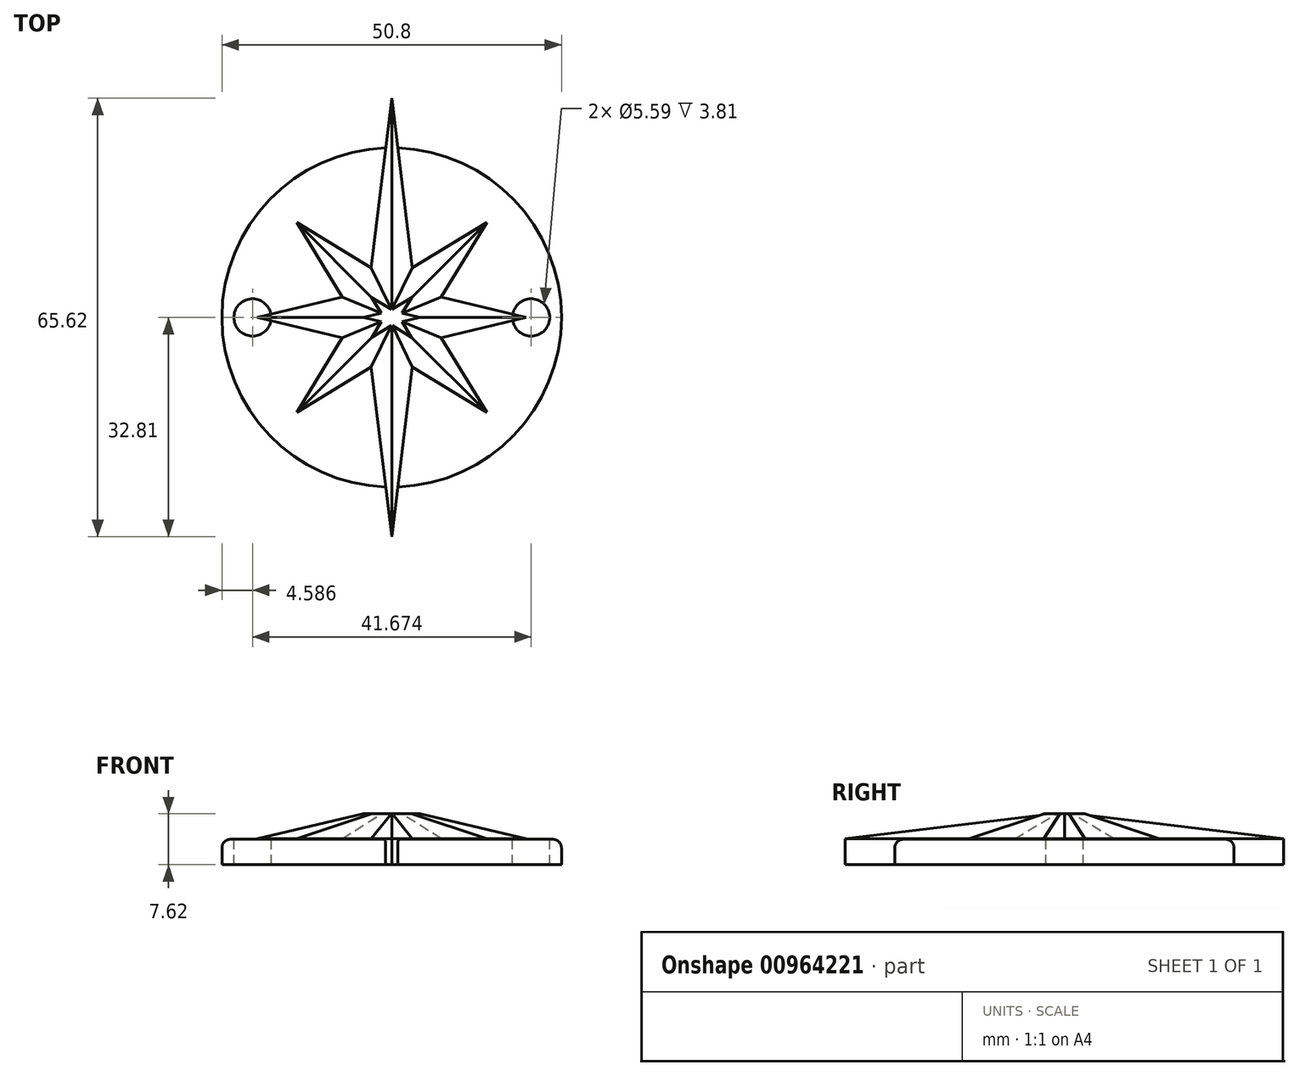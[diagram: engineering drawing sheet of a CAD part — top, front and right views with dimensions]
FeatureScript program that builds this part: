
annotation { "Feature Type Name" : "Feature", "Feature Type Description" : "" }
export const myFeature = defineFeature(function(context is Context, id is Id, definition is map)
    precondition{}
    {
        {
            var Q0;
            Q0=qCreatedBy(makeId("Top.planeOp"),FACE);
            var sketch = newSketch(context, id + "F0", { "sketchPlane" : qUnion([Q0])});
            skCircle(sketch, "E0.cCircle", {"center": v(0, 0) * mm, "radius": 7.42 * mm, "construction": true});
            skLineSegment(sketch, "E0.0", {"start": v(3.07, 7.42) * mm, "end": v(7.42, 3.07) * mm});
            skLineSegment(sketch, "E0.1", {"start": v(7.42, 3.07) * mm, "end": v(7.42, -3.07) * mm});
            skLineSegment(sketch, "E0.2", {"start": v(7.42, -3.07) * mm, "end": v(3.07, -7.42) * mm});
            skLineSegment(sketch, "E0.3", {"start": v(3.07, -7.42) * mm, "end": v(-3.07, -7.42) * mm});
            skLineSegment(sketch, "E0.4", {"start": v(-3.07, -7.42) * mm, "end": v(-7.42, -3.07) * mm});
            skLineSegment(sketch, "E0.5", {"start": v(-7.42, -3.07) * mm, "end": v(-7.42, 3.07) * mm});
            skLineSegment(sketch, "E0.6", {"start": v(-7.42, 3.07) * mm, "end": v(-3.07, 7.42) * mm});
            skLineSegment(sketch, "E0.7", {"start": v(-3.07, 7.42) * mm, "end": v(3.07, 7.42) * mm});
            skPoint(sketch, "E0.0.midPoint", {"position": v(5.24, 5.24) * mm});
            skSolve(sketch);
        }
        {
            var Q0;
            Q0=qCreatedBy(makeId("Top.planeOp"),FACE);
            var sketch = newSketch(context, id + "F1", { "sketchPlane" : qUnion([Q0])});
            skLineSegment(sketch, "E1", {"start": v(0, -32.8) * mm, "end": v(3.07, -7.42) * mm});
            skLineSegment(sketch, "E2", {"start": v(3.07, -7.42) * mm, "end": v(14.23, -14.23) * mm});
            skLineSegment(sketch, "E3", {"start": v(14.23, -14.23) * mm, "end": v(7.4, -3.07) * mm});
            skLineSegment(sketch, "E4", {"start": v(7.4, -3.07) * mm, "end": v(20.12, 0) * mm});
            skLineSegment(sketch, "E5", {"start": v(20.12, 0) * mm, "end": v(7.42, 3.07) * mm});
            skLineSegment(sketch, "E6", {"start": v(7.42, 3.07) * mm, "end": v(14.22, 14.22) * mm});
            skLineSegment(sketch, "E7", {"start": v(14.22, 14.22) * mm, "end": v(3.07, 7.41) * mm});
            skLineSegment(sketch, "E8", {"start": v(3.07, 7.41) * mm, "end": v(0, 32.8) * mm});
            skLineSegment(sketch, "E9", {"start": v(0, 32.8) * mm, "end": v(-3.07, 7.42) * mm});
            skLineSegment(sketch, "E10", {"start": v(-3.07, 7.42) * mm, "end": v(-14.22, 14.23) * mm});
            skLineSegment(sketch, "E11", {"start": v(-14.22, 14.23) * mm, "end": v(-7.41, 3.07) * mm});
            skLineSegment(sketch, "E12", {"start": v(-7.41, 3.07) * mm, "end": v(-20.12, 0) * mm});
            skLineSegment(sketch, "E13", {"start": v(-20.12, 0) * mm, "end": v(-7.4, -3.07) * mm});
            skLineSegment(sketch, "E14", {"start": v(-7.4, -3.07) * mm, "end": v(-14.22, -14.2) * mm});
            skLineSegment(sketch, "E15", {"start": v(-14.22, -14.2) * mm, "end": v(-3.07, -7.42) * mm});
            skLineSegment(sketch, "E16", {"start": v(-3.07, -7.42) * mm, "end": v(0, -32.8) * mm});
            skSolve(sketch);
        }
        {
            var Q0;
            Q0 = qSketchRegion(id + "F1", true);
            extrude(context, id + "F2", {"entities" : qUnion([Q0]), "depth" : 7.62 * mm, "offsetDistance" : 25.4 * mm});
        }
        {
            var Q0;
            Q0=qCreatedBy(makeId("Top.planeOp"),FACE);
            var sketch = newSketch(context, id + "F3", { "sketchPlane" : qUnion([Q0])});
            skCircle(sketch, "E17", {"center": v(0, 0) * mm, "radius": 25.4 * mm});
            skSolve(sketch);
        }
        {
            var Q0;
            Q0=makeQuery(id+"F3.imprint","IMPRINT",FACE,{"disambiguationData":[TD([[makeQuery(id+"F3.imprint","IMPRINT",EDGE,{"derivedFrom":sQuery(id+"F3.wireOp",EDGE,"E17")}),1.0]])]});
            extrude(context, id + "F4", {"entities" : qUnion([Q0]), "operationType" : NewBodyOperationType.ADD, "depth" : 3.8 * mm, "offsetDistance" : 25.4 * mm});
        }
        {
            var Q0;
            Q0=makeQuery(id+"F2.opExtrude","CAP_FACE",FACE,{"disambiguationData":[OSD([sQuery(id+"F1.wireOp",EDGE,"E1"),sQuery(id+"F1.wireOp",EDGE,"E2"),sQuery(id+"F1.wireOp",EDGE,"E3"),sQuery(id+"F1.wireOp",EDGE,"E4"),sQuery(id+"F1.wireOp",EDGE,"E5"),sQuery(id+"F1.wireOp",EDGE,"E6"),sQuery(id+"F1.wireOp",EDGE,"E7"),sQuery(id+"F1.wireOp",EDGE,"E8"),sQuery(id+"F1.wireOp",EDGE,"E9"),sQuery(id+"F1.wireOp",EDGE,"E10"),sQuery(id+"F1.wireOp",EDGE,"E11"),sQuery(id+"F1.wireOp",EDGE,"E12"),sQuery(id+"F1.wireOp",EDGE,"E13"),sQuery(id+"F1.wireOp",EDGE,"E14"),sQuery(id+"F1.wireOp",EDGE,"E15"),sQuery(id+"F1.wireOp",EDGE,"E16")])],"isStart":false});
            chamfer(context, id + "F5", {"entities" : qUnion([Q0]), "width" : 3.73 * mm, "tangentPropagation" : true});
        }
        {
            var Q0;
            {var subQ0=sQuery(id+"F3.wireOp",EDGE,"E17");Q0=makeQuery(id+"F4.boolean.opBoolean","SPLIT",EDGE,{"disambiguationData":[TD([makeQuery(id+"F2.opExtrude","SWEPT_FACE",FACE,{"disambiguationData":[OSD([sQuery(id+"F1.wireOp",EDGE,"E1")])]})])],"derivedFrom":makeQuery(id+"F4.opExtrude","CAP_EDGE",EDGE,{"disambiguationData":[OSD([subQ0])],"isStart":false})});}
            var Q1;
            {var subQ0=sQuery(id+"F3.wireOp",EDGE,"E17");Q1=makeQuery(id+"F4.boolean.opBoolean","SPLIT",EDGE,{"disambiguationData":[TD([makeQuery(id+"F2.opExtrude","SWEPT_FACE",FACE,{"disambiguationData":[OSD([sQuery(id+"F1.wireOp",EDGE,"E9")])]})])],"derivedFrom":makeQuery(id+"F4.opExtrude","CAP_EDGE",EDGE,{"disambiguationData":[OSD([subQ0])],"isStart":false})});}
            fillet(context, id + "F6", {"entities" : qUnion([Q0, Q1]), "radius" : 1.27 * mm, "tangentPropagation" : true, "allowEdgeOverflow" : false});
        }
        {
            var Q0;
            {var subQ0=sQuery(id+"F3.wireOp",EDGE,"E17");Q0=makeQuery(id+"F4.boolean.opBoolean","SPLIT",FACE,{"disambiguationData":[TD([makeQuery(id+"F2.opExtrude","SWEPT_FACE",FACE,{"disambiguationData":[OSD([sQuery(id+"F1.wireOp",EDGE,"E1")])]})])],"derivedFrom":makeQuery(id+"F4.opExtrude","CAP_FACE",FACE,{"disambiguationData":[OSD([subQ0])],"isStart":false})});}
            cPlane(context, id + "F7", {"entities" : qUnion([Q0]), "cplaneType" : CPlaneType.OFFSET, "offset" : 0 * mm, "width" : 152.4 * mm, "height" : 152.4 * mm});
        }
        {
            var Q0;
            Q0=qCreatedBy(id+"F7.planeOp",FACE);
            var sketch = newSketch(context, id + "F8", { "sketchPlane" : qUnion([Q0])});
            skPoint(sketch, "E18", {"position": v(-20.81, 0) * mm});
            skPoint(sketch, "E19", {"position": v(20.86, 0) * mm});
            skSolve(sketch);
        }
        {
            var Q0;
            Q0=sQuery(id+"F8.wireOp",VERTEX,"E18");
            var Q1;
            Q1=sQuery(id+"F8.wireOp",VERTEX,"E19");
            var Q2;
            Q2=makeQuery(id+"F2.opExtrude","SWEPT_BODY",BODY,{"disambiguationData":[OSD([sQuery(id+"F1.wireOp",EDGE,"E1"),sQuery(id+"F1.wireOp",EDGE,"E2"),sQuery(id+"F1.wireOp",EDGE,"E3"),sQuery(id+"F1.wireOp",EDGE,"E4"),sQuery(id+"F1.wireOp",EDGE,"E5"),sQuery(id+"F1.wireOp",EDGE,"E6"),sQuery(id+"F1.wireOp",EDGE,"E7"),sQuery(id+"F1.wireOp",EDGE,"E8"),sQuery(id+"F1.wireOp",EDGE,"E9"),sQuery(id+"F1.wireOp",EDGE,"E10"),sQuery(id+"F1.wireOp",EDGE,"E11"),sQuery(id+"F1.wireOp",EDGE,"E12"),sQuery(id+"F1.wireOp",EDGE,"E13"),sQuery(id+"F1.wireOp",EDGE,"E14"),sQuery(id+"F1.wireOp",EDGE,"E15"),sQuery(id+"F1.wireOp",EDGE,"E16")])]});
            hole(context, id + "F9", {"style" : HoleStyle.SIMPLE, "endStyle" : HoleEndStyle.BLIND, "holeDiameter" : 5.6 * mm, "majorDiameter" : 6.35 * mm, "holeDepth" : 127 * mm, "isTappedThrough" : true, "tappedDepth" : 12.7 * mm, "tapClearance" : 3, "startFromSketch" : true, "locations" : qUnion([Q0, Q1]), "scope" : qUnion([Q2])});
        }
    });
